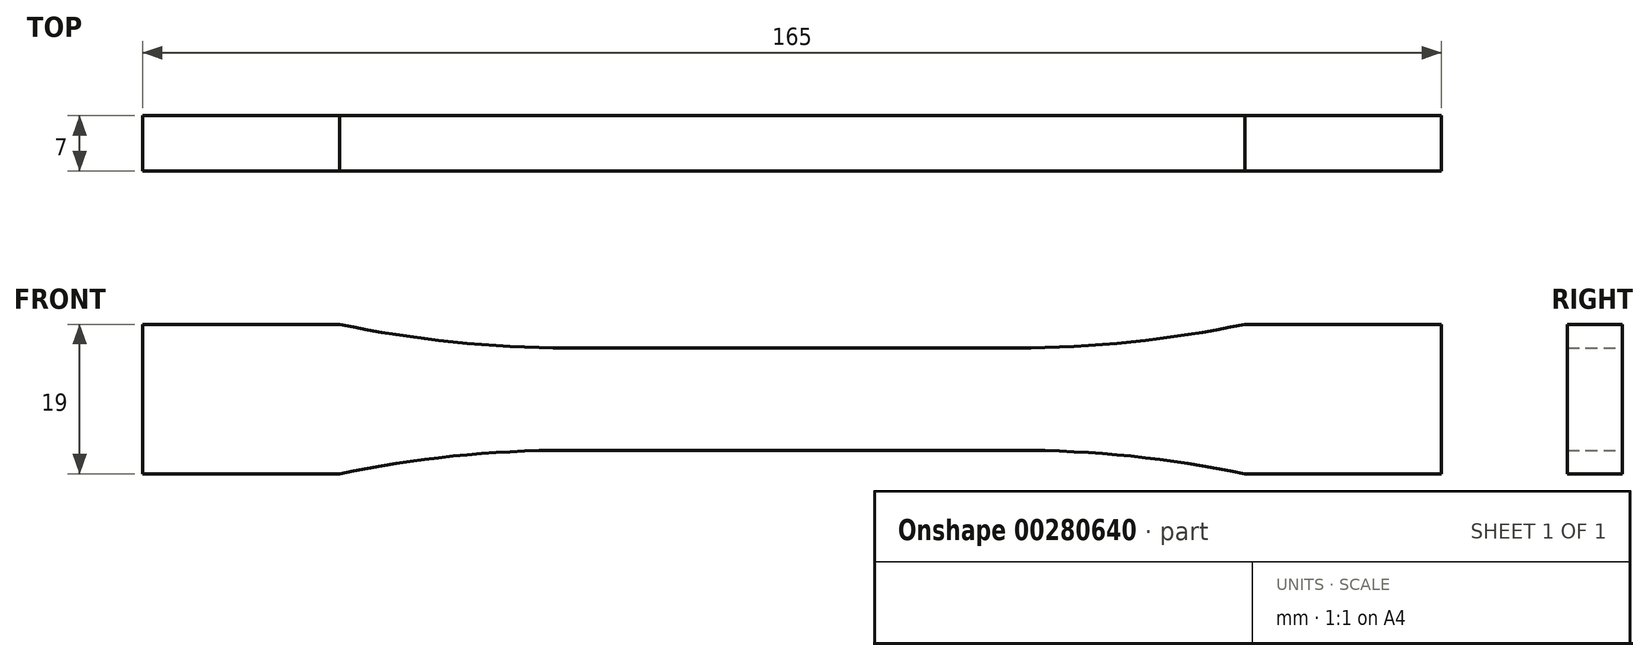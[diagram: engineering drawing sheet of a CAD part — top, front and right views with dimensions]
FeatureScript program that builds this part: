
annotation { "Feature Type Name" : "Feature", "Feature Type Description" : "" }
export const myFeature = defineFeature(function(context is Context, id is Id, definition is map)
    precondition{}
    {
        {
            var Q0;
            Q0=qCreatedBy(makeId("Front.planeOp"),FACE);
            var sketch = newSketch(context, id + "F0", { "sketchPlane" : qUnion([Q0])});
            skLineSegment(sketch, "E0", {"start": v(0, 6.5) * mm, "end": v(28.5, 6.5) * mm});
            skArc(sketch, "E1", {"start": v(28.5, 6.5) * mm, "mid": v(43.08, 7.25) * mm, "end": v(57.5, 9.5) * mm});
            skLineSegment(sketch, "E2", {"start": v(57.5, 9.5) * mm, "end": v(82.5, 9.5) * mm});
            skLineSegment(sketch, "E3", {"start": v(82.5, 9.5) * mm, "end": v(82.5, 0) * mm});
            skLineSegment(sketch, "E4.MirrorCS", {"start": v(0, 6.5) * mm, "end": v(-28.5, 6.5) * mm});
            skLineSegment(sketch, "E5.MirrorCS", {"start": v(-82.5, 9.5) * mm, "end": v(-82.5, 0) * mm});
            skLineSegment(sketch, "E6.MirrorCS", {"start": v(-57.5, 9.5) * mm, "end": v(-82.5, 9.5) * mm});
            skArc(sketch, "E7.MirrorCS", {"start": v(-28.5, 6.5) * mm, "mid": v(-43.08, 7.25) * mm, "end": v(-57.5, 9.5) * mm});
            skLineSegment(sketch, "E8.MirrorCS", {"start": v(0, -6.5) * mm, "end": v(28.5, -6.5) * mm});
            skArc(sketch, "E9.MirrorCS", {"start": v(28.5, -6.5) * mm, "mid": v(43.08, -7.25) * mm, "end": v(57.5, -9.5) * mm});
            skLineSegment(sketch, "E10.MirrorCS", {"start": v(57.5, -9.5) * mm, "end": v(82.5, -9.5) * mm});
            skLineSegment(sketch, "E11.MirrorCS", {"start": v(82.5, -9.5) * mm, "end": v(82.5, 0) * mm});
            skLineSegment(sketch, "E12.MirrorCS", {"start": v(0, -6.5) * mm, "end": v(-28.5, -6.5) * mm});
            skLineSegment(sketch, "E13.MirrorCS", {"start": v(-57.5, -9.5) * mm, "end": v(-82.5, -9.5) * mm});
            skLineSegment(sketch, "E14.MirrorCS", {"start": v(-82.5, -9.5) * mm, "end": v(-82.5, 0) * mm});
            skArc(sketch, "E15.MirrorCS", {"start": v(-28.5, -6.5) * mm, "mid": v(-43.08, -7.25) * mm, "end": v(-57.5, -9.5) * mm});
            skSolve(sketch);
        }
        {
            var Q0;
            Q0=makeQuery(id+"F0.imprint","IMPRINT",FACE,{"disambiguationData":[TD([[makeQuery(id+"F0.imprint","IMPRINT",EDGE,{"derivedFrom":sQuery(id+"F0.wireOp",EDGE,"E0")}),-1.0]])]});
            extrude(context, id + "F1", {"entities" : qUnion([Q0]), "endBound" : BoundingType.SYMMETRIC, "depth" : 7 * mm});
        }
    });
